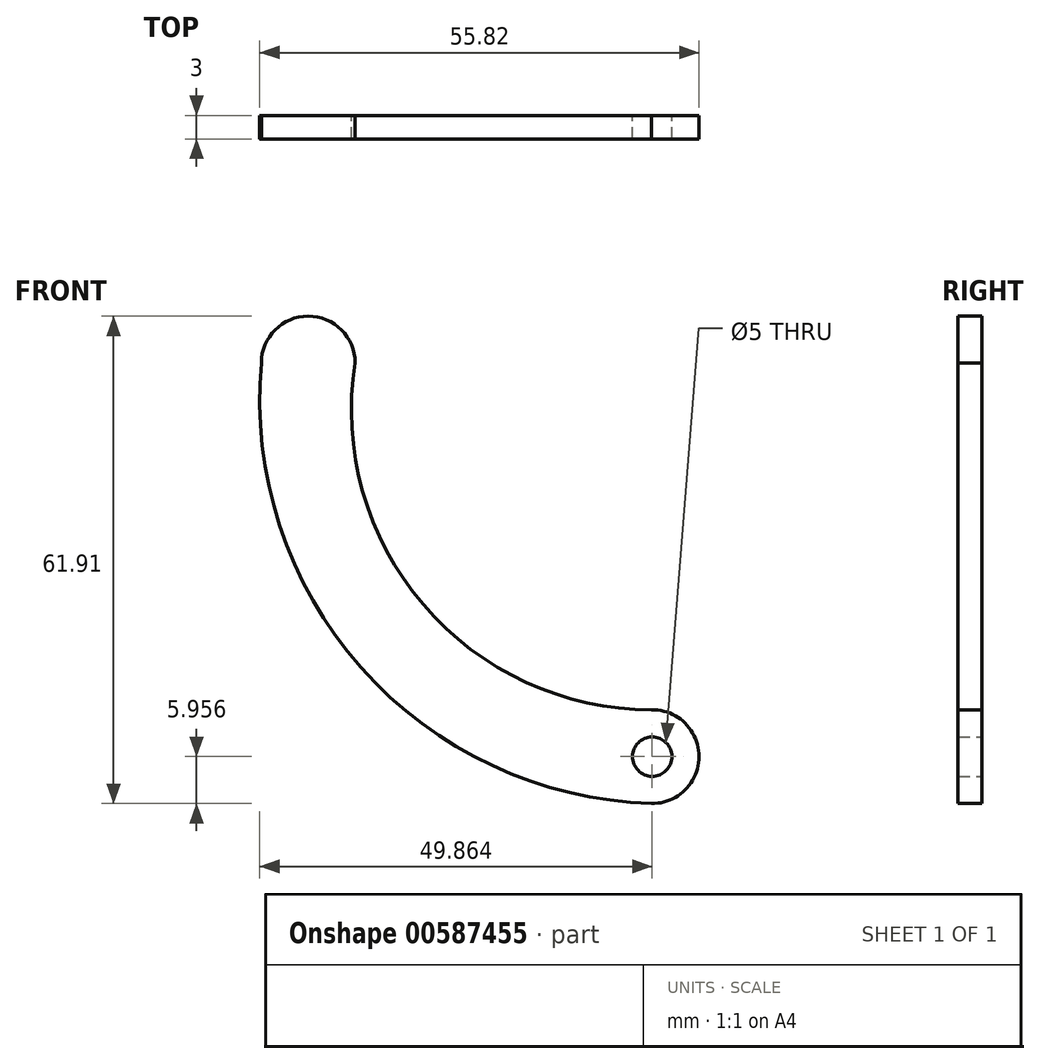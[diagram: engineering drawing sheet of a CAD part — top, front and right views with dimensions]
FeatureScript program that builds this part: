
annotation { "Feature Type Name" : "Feature", "Feature Type Description" : "" }
export const myFeature = defineFeature(function(context is Context, id is Id, definition is map)
    precondition{}
    {
        {
            var Q0;
            Q0=qCreatedBy(makeId("Front.planeOp"),FACE);
            var sketch = newSketch(context, id + "F0", { "sketchPlane" : qUnion([Q0])});
            skArc(sketch, "E0", {"start": v(-66.66, 53.3) * mm, "mid": v(-53.98, 14.6) * mm, "end": v(-17.09, -2.65) * mm});
            skArc(sketch, "E1", {"start": v(-17.09, -2.65) * mm, "mid": v(-11.05, 3.3) * mm, "end": v(-17.09, 9.26) * mm});
            skArc(sketch, "E2", {"start": v(-54.75, 53.3) * mm, "mid": v(-60.7, 59.26) * mm, "end": v(-66.66, 53.3) * mm});
            skArc(sketch, "E3", {"start": v(-54.75, 53.3) * mm, "mid": v(-46.07, 22.6) * mm, "end": v(-17.09, 9.26) * mm});
            skCircle(sketch, "E4", {"center": v(-17, 3.3) * mm, "radius": 2.5 * mm});
            skSolve(sketch);
        }
        {
            var Q0;
            Q0 = qSketchRegion(id + "F0", true);
            extrude(context, id + "F1", {"entities" : qUnion([Q0]), "depth" : 3 * mm, "offsetDistance" : 25 * mm});
        }
    });
